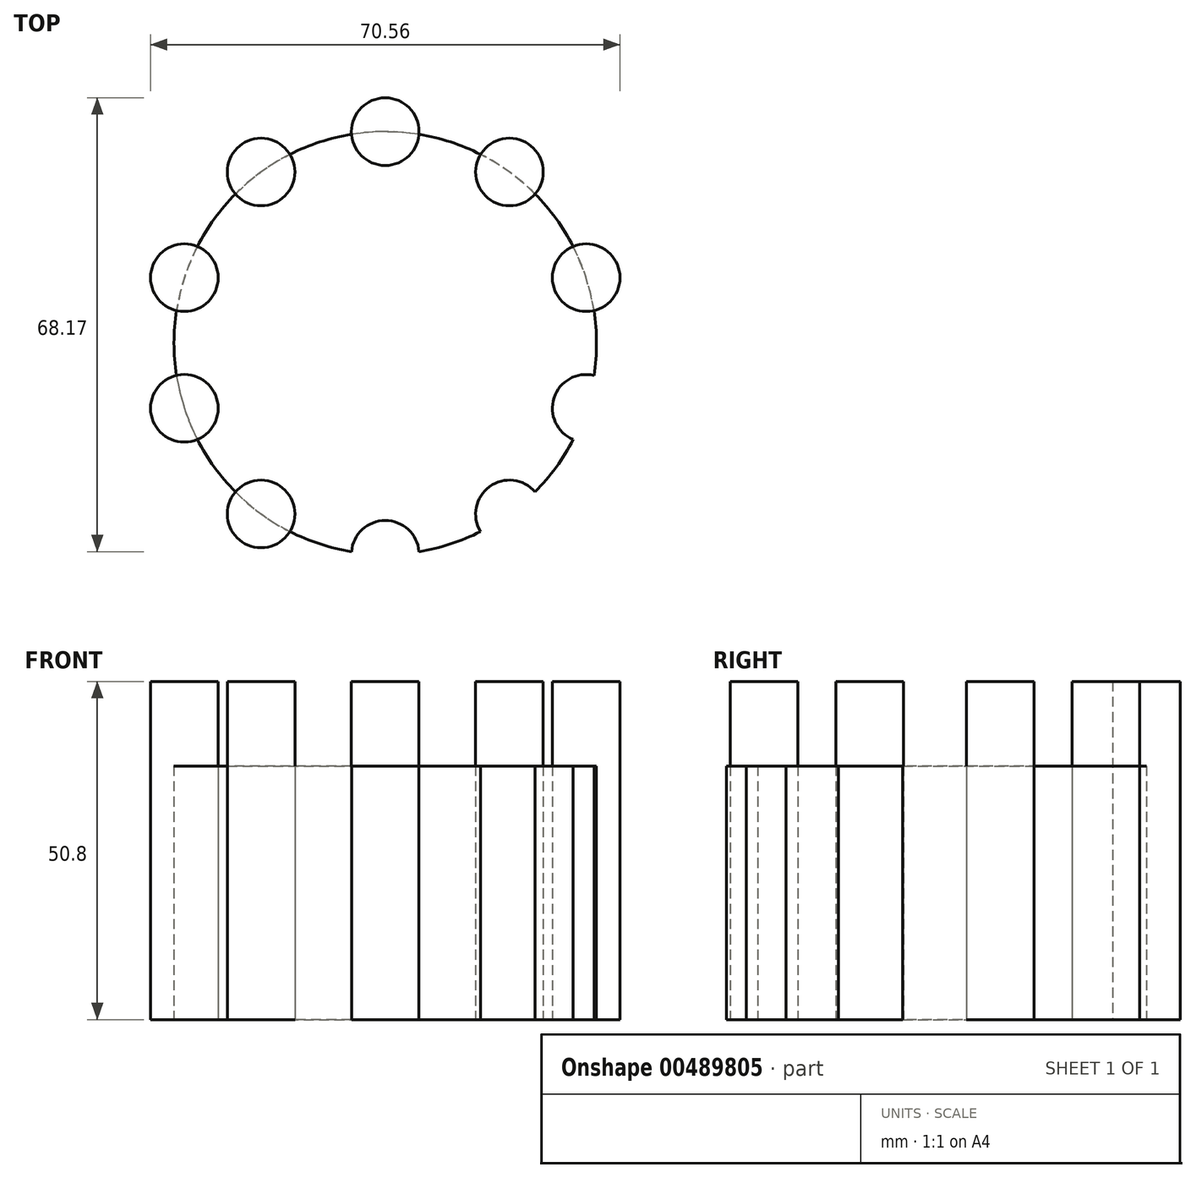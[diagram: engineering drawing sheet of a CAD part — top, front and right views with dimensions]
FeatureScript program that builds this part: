
annotation { "Feature Type Name" : "Feature", "Feature Type Description" : "" }
export const myFeature = defineFeature(function(context is Context, id is Id, definition is map)
    precondition{}
    {
        {
            var Q0;
            Q0=qCreatedBy(makeId("Top.planeOp"),FACE);
            var sketch = newSketch(context, id + "F0", { "sketchPlane" : qUnion([Q0])});
            skCircle(sketch, "E0", {"center": v(0, 0) * mm, "radius": 31.75 * mm});
            skSolve(sketch);
        }
        {
            var Q0;
            Q0=makeQuery(id+"F0.imprint","IMPRINT",FACE,{"disambiguationData":[TD([[makeQuery(id+"F0.imprint","IMPRINT",EDGE,{"derivedFrom":sQuery(id+"F0.wireOp",EDGE,"E0")}),1.0]])]});
            extrude(context, id + "F1", {"entities" : qUnion([Q0]), "depth" : 38.1 * mm});
        }
        {
            var Q0;
            Q0=qCreatedBy(makeId("Top.planeOp"),FACE);
            var sketch = newSketch(context, id + "F2", { "sketchPlane" : qUnion([Q0])});
            skCircle(sketch, "E1", {"center": v(0, 31.75) * mm, "radius": 5.08 * mm});
            skCircle(sketch, "E2.1.0", {"center": v(-18.66, 25.69) * mm, "radius": 5.08 * mm});
            skCircle(sketch, "E2.2.0", {"center": v(-30.2, 9.81) * mm, "radius": 5.08 * mm});
            skCircle(sketch, "E2.3.0", {"center": v(-30.2, -9.81) * mm, "radius": 5.08 * mm});
            skCircle(sketch, "E2.4.0", {"center": v(-18.66, -25.69) * mm, "radius": 5.08 * mm});
            skCircle(sketch, "E2.5.0", {"center": v(0, -31.75) * mm, "radius": 5.08 * mm});
            skCircle(sketch, "E2.6.0", {"center": v(18.66, -25.69) * mm, "radius": 5.08 * mm});
            skCircle(sketch, "E2.7.0", {"center": v(30.2, -9.81) * mm, "radius": 5.08 * mm});
            skCircle(sketch, "E2.8.0", {"center": v(30.2, 9.81) * mm, "radius": 5.08 * mm});
            skCircle(sketch, "E2.9.0", {"center": v(18.66, 25.69) * mm, "radius": 5.08 * mm});
            skPoint(sketch, "E2.center", {"position": v(0, 0) * mm});
            skSolve(sketch);
        }
        {
            var Q0;
            Q0=qSketchRegion(id+"F2",true);
            extrude(context, id + "F3", {"entities" : qUnion([Q0]), "depth" : 50.8 * mm});
        }
        {
            var Q0;
            Q0=makeQuery(id+"F3.opExtrude","SWEPT_BODY",BODY,{"disambiguationData":[OSD([sQuery(id+"F2.wireOp",EDGE,"E2.7.0")])]});
            var Q1;
            Q1=makeQuery(id+"F3.opExtrude","SWEPT_BODY",BODY,{"disambiguationData":[OSD([sQuery(id+"F2.wireOp",EDGE,"E2.6.0")])]});
            var Q2;
            Q2=makeQuery(id+"F3.opExtrude","SWEPT_BODY",BODY,{"disambiguationData":[OSD([sQuery(id+"F2.wireOp",EDGE,"E2.5.0")])]});
            var Q3;
            Q3=makeQuery(id+"F1.opExtrude","SWEPT_BODY",BODY,{"disambiguationData":[OSD([sQuery(id+"F0.wireOp",EDGE,"E0")])]});
            booleanBodies(context, id + "F4", {"operationType" : BooleanOperationType.SUBTRACTION, "tools" : qUnion([Q0, Q1, Q2]), "targets" : qUnion([Q3])});
        }
    });
